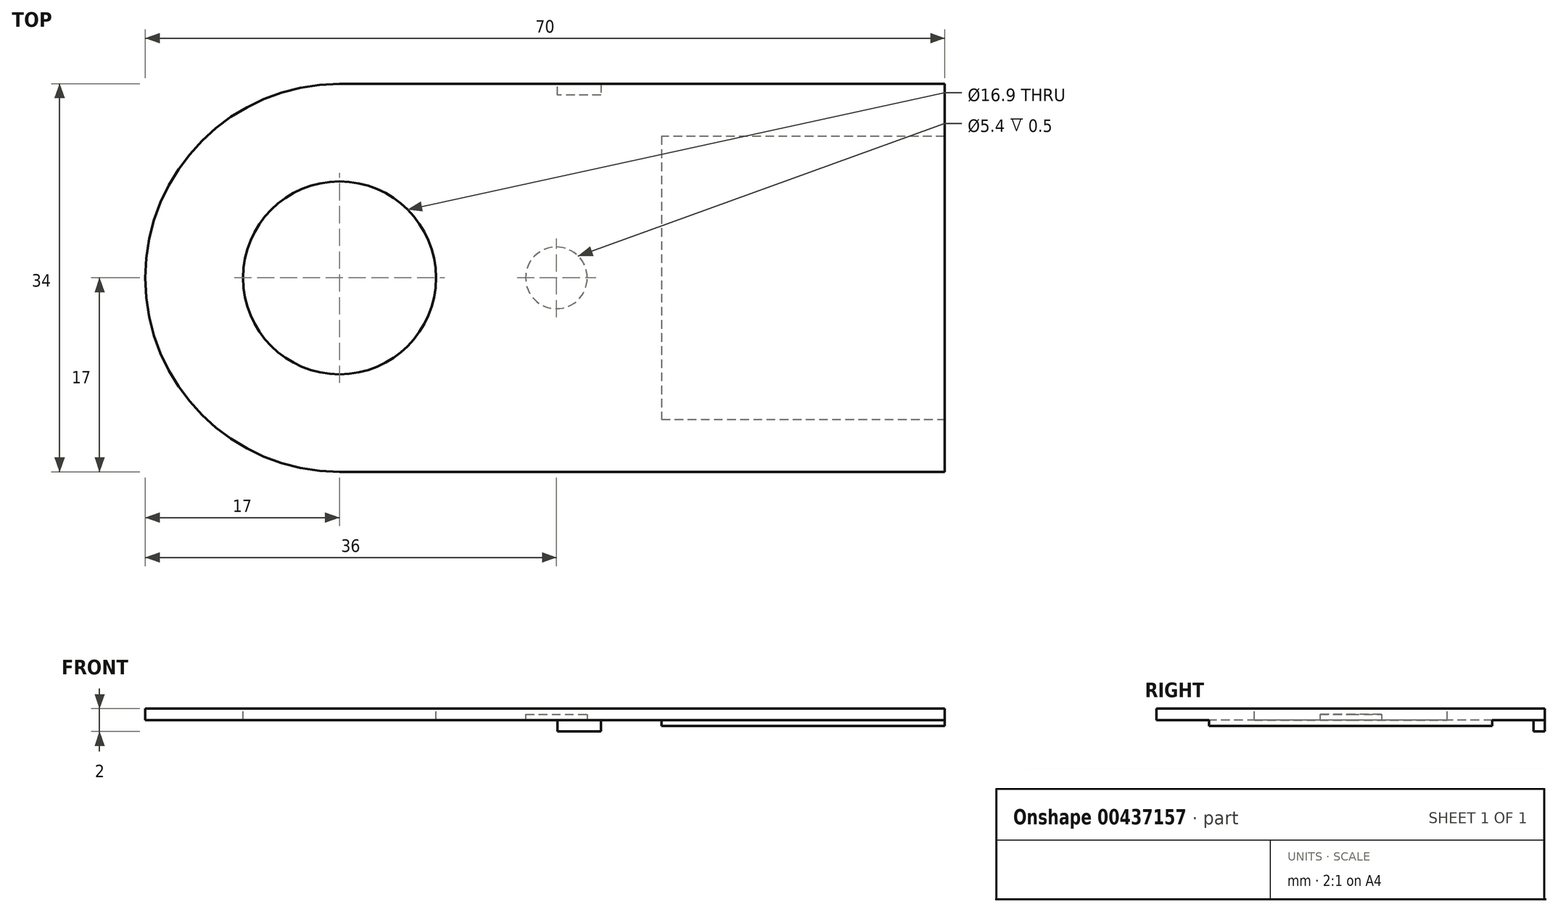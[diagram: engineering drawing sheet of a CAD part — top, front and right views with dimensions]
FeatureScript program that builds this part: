
annotation { "Feature Type Name" : "Feature", "Feature Type Description" : "" }
export const myFeature = defineFeature(function(context is Context, id is Id, definition is map)
    precondition{}
    {
        {
            var Q0;
            Q0=qCreatedBy(makeId("Top.planeOp"),FACE);
            var sketch = newSketch(context, id + "F0", { "sketchPlane" : qUnion([Q0])});
            skLineSegment(sketch, "E0", {"start": v(0, 17) * mm, "end": v(53, 17) * mm});
            skLineSegment(sketch, "E1", {"start": v(53, 17) * mm, "end": v(53, -17) * mm});
            skLineSegment(sketch, "E2", {"start": v(53, -17) * mm, "end": v(0, -17) * mm});
            skArc(sketch, "E3", {"start": v(0, -17) * mm, "mid": v(-17, 0) * mm, "end": v(0, 17) * mm});
            skCircle(sketch, "E4", {"center": v(0, 0) * mm, "radius": 8.45 * mm});
            skLineSegment(sketch, "E5", {"start": v(19.1, 17) * mm, "end": v(19.1, 16) * mm});
            skLineSegment(sketch, "E6", {"start": v(19.1, 16) * mm, "end": v(22.9, 16) * mm});
            skLineSegment(sketch, "E7", {"start": v(22.9, 16) * mm, "end": v(22.9, 17) * mm});
            skLineSegment(sketch, "E8", {"start": v(53, 12.4) * mm, "end": v(28.2, 12.4) * mm});
            skLineSegment(sketch, "E9", {"start": v(28.2, 12.4) * mm, "end": v(28.2, -12.4) * mm});
            skLineSegment(sketch, "E10", {"start": v(28.2, -12.4) * mm, "end": v(53, -12.4) * mm});
            skSolve(sketch);
        }
        {
            var Q0;
            {var subQ0=sQuery(id+"F0.wireOp",EDGE,"E5");Q0=makeQuery(id+"F0.imprint","IMPRINT",FACE,{"disambiguationData":[TD([[makeQuery(id+"F0.imprint","IMPRINT",EDGE,{"derivedFrom":subQ0}),1.0]])]});}
            extrude(context, id + "F1", {"entities" : qUnion([Q0]), "oppositeDirection" : true, "depth" : 2 * mm});
        }
        {
            var Q0;
            Q0 = qSketchRegion(id + "F0", true);
            extrude(context, id + "F2", {"entities" : qUnion([Q0]), "operationType" : NewBodyOperationType.ADD, "oppositeDirection" : true, "depth" : 1 * mm});
        }
        {
            var Q0;
            Q0=makeQuery(id+"F2.opExtrude","CAP_FACE",FACE,{"disambiguationData":[OSD([sQuery(id+"F0.wireOp",EDGE,"E0"),sQuery(id+"F0.wireOp",EDGE,"E1"),sQuery(id+"F0.wireOp",EDGE,"E2"),sQuery(id+"F0.wireOp",EDGE,"E3"),sQuery(id+"F0.wireOp",EDGE,"E4")])],"isStart":false});
            var sketch = newSketch(context, id + "F3", { "sketchPlane" : qUnion([Q0])});
            skPoint(sketch, "E11", {"position": v(19, 0) * mm});
            skCircle(sketch, "E12", {"center": v(19, 0) * mm, "radius": 2.7 * mm});
            skSolve(sketch);
        }
        {
            var Q0;
            Q0=makeQuery(id+"F3.imprint","IMPRINT",FACE,{"disambiguationData":[TD([[makeQuery(id+"F3.imprint","IMPRINT",EDGE,{"derivedFrom":sQuery(id+"F3.wireOp",EDGE,"E12")}),1.0]])]});
            extrude(context, id + "F4", {"entities" : qUnion([Q0]), "operationType" : NewBodyOperationType.REMOVE, "oppositeDirection" : true, "depth" : 0.5 * mm});
        }
        {
            var Q0;
            {var subQ0=sQuery(id+"F0.wireOp",EDGE,"E8");Q0=makeQuery(id+"F0.imprint","IMPRINT",FACE,{"disambiguationData":[TD([[makeQuery(id+"F0.imprint","IMPRINT",EDGE,{"derivedFrom":subQ0}),1.0]])]});}
            extrude(context, id + "F5", {"entities" : qUnion([Q0]), "operationType" : NewBodyOperationType.ADD, "oppositeDirection" : true, "depth" : 1.5 * mm});
        }
    });
